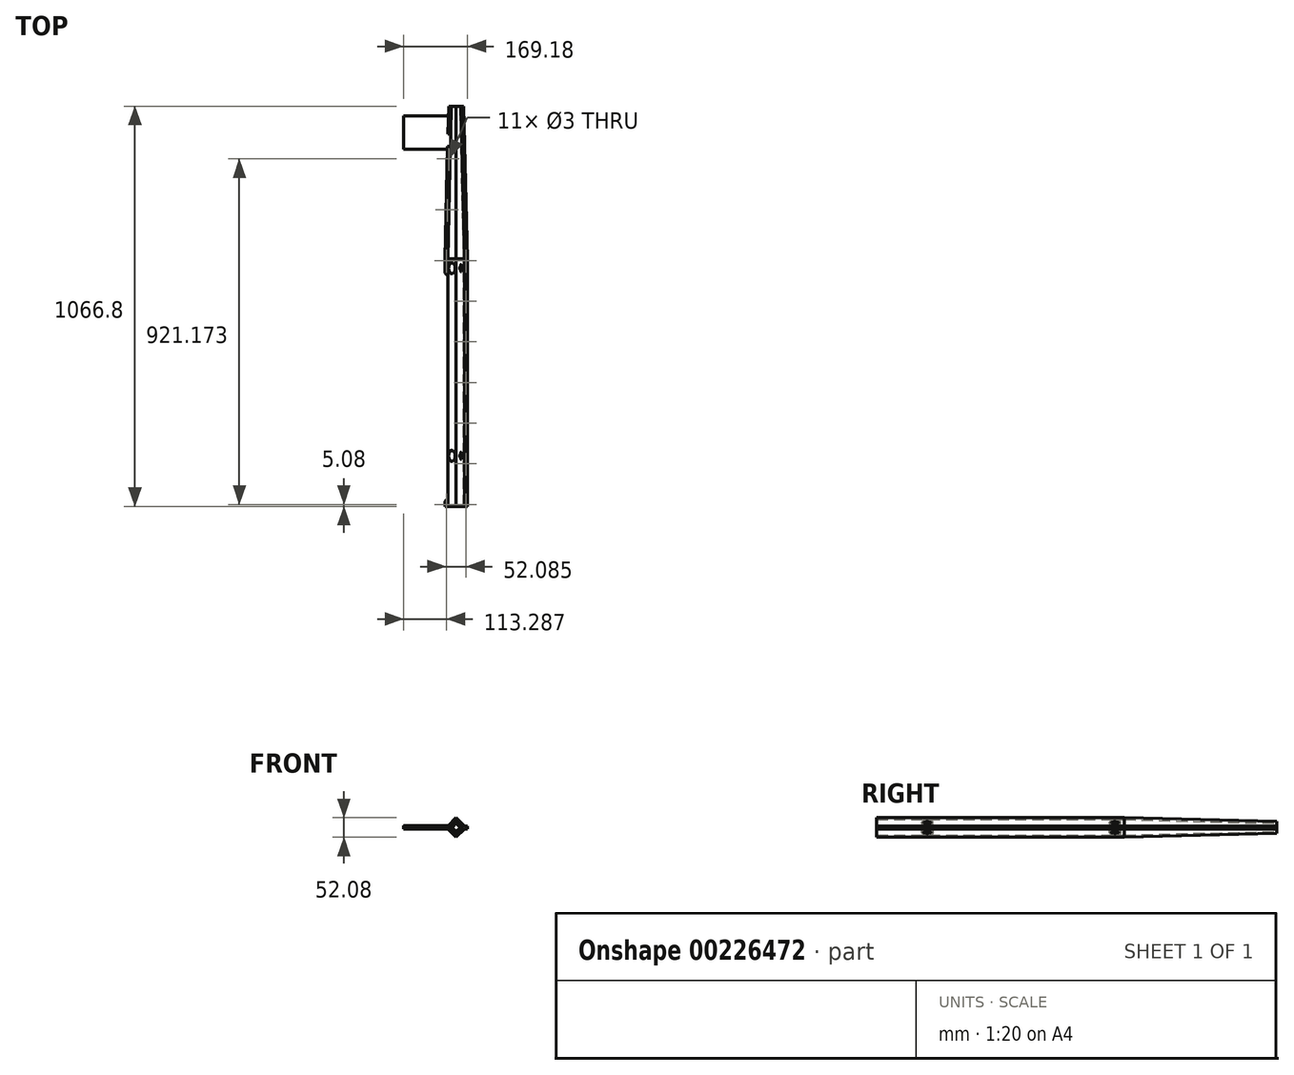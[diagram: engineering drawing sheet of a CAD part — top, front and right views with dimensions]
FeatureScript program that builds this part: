
annotation { "Feature Type Name" : "Feature", "Feature Type Description" : "" }
export const myFeature = defineFeature(function(context is Context, id is Id, definition is map)
    precondition{}
    {
        {
            var Q0;
            Q0=qCreatedBy(makeId("Front.planeOp"),FACE);
            var sketch = newSketch(context, id + "F0", { "sketchPlane" : qUnion([Q0])});
            skLineSegment(sketch, "E0", {"start": v(0, 0) * mm, "end": v(0, -26.04) * mm, "construction": true});
            skLineSegment(sketch, "E1", {"start": v(0, -20.65) * mm, "end": v(-20.65, 0) * mm});
            skLineSegment(sketch, "E2", {"start": v(0, -26.04) * mm, "end": v(-22.23, -3.81) * mm});
            skLineSegment(sketch, "E3", {"start": v(-22.23, -3.8) * mm, "end": v(-29.85, -3.81) * mm});
            skLineSegment(sketch, "E4", {"start": v(-29.85, -3.81) * mm, "end": v(-29.85, 0) * mm});
            skLineSegment(sketch, "E5", {"start": v(-29.85, 0) * mm, "end": v(-20.65, 0) * mm});
            skLineSegment(sketch, "E6.MirrorCS", {"start": v(29.85, -3.8) * mm, "end": v(29.85, 0) * mm});
            skLineSegment(sketch, "E7.MirrorCS", {"start": v(29.85, 0) * mm, "end": v(20.65, 0) * mm});
            skLineSegment(sketch, "E8.MirrorCS", {"start": v(0, -20.65) * mm, "end": v(20.65, 0) * mm});
            skLineSegment(sketch, "E9.MirrorCS", {"start": v(22.23, -3.8) * mm, "end": v(29.85, -3.8) * mm});
            skLineSegment(sketch, "E10.MirrorCS", {"start": v(0, -26.04) * mm, "end": v(22.23, -3.8) * mm});
            skSolve(sketch);
        }
        {
            var Q0;
            Q0=makeQuery(id+"F0.imprint","IMPRINT",FACE,{"disambiguationData":[TD([[makeQuery(id+"F0.imprint","IMPRINT",EDGE,{"derivedFrom":sQuery(id+"F0.wireOp",EDGE,"E1")}),1.0]])]});
            extrude(context, id + "F1", {"entities" : qUnion([Q0]), "depth" : 660.4 * mm});
        }
        {
            var Q0;
            Q0=makeQuery(id+"F1.opExtrude","SWEPT_FACE",FACE,{"disambiguationData":[OSD([sQuery(id+"F0.wireOp",EDGE,"E2")])]});
            var sketch = newSketch(context, id + "F2", { "sketchPlane" : qUnion([Q0])});
            skCircle(sketch, "E11", {"center": v(525.78, -0.79) * mm, "radius": 14.5 * mm});
            skCircle(sketch, "E12", {"center": v(25.4, -0.79) * mm, "radius": 14.5 * mm});
            skPoint(sketch, "E13.0", {"position": v(660.4, -14.6) * mm});
            skLineSegment(sketch, "E14", {"start": v(660.4, -14.6) * mm, "end": v(660.4, 13.03) * mm, "construction": true});
            skLineSegment(sketch, "E15", {"start": v(660.4, -0.79) * mm, "end": v(-254, -0.79) * mm, "construction": true});
            skSolve(sketch);
        }
        {
            var Q0;
            Q0=makeQuery(id+"F2.imprint","IMPRINT",FACE,{"disambiguationData":[TD([[makeQuery(id+"F2.imprint","IMPRINT",EDGE,{"derivedFrom":sQuery(id+"F2.wireOp",EDGE,"E11")}),1.0]])]});
            var Q1;
            Q1=makeQuery(id+"F2.imprint","IMPRINT",FACE,{"disambiguationData":[TD([[makeQuery(id+"F2.imprint","IMPRINT",EDGE,{"derivedFrom":sQuery(id+"F2.wireOp",EDGE,"E12")}),1.0]])]});
            var Q2;
            Q2=makeQuery(id+"F1.opExtrude","SWEPT_FACE",FACE,{"disambiguationData":[OSD([sQuery(id+"F0.wireOp",EDGE,"E1")])]});
            extrude(context, id + "F3", {"entities" : qUnion([Q0, Q1]), "operationType" : NewBodyOperationType.REMOVE, "endBound" : BoundingType.UP_TO_SURFACE, "oppositeDirection" : true, "endBoundEntityFace" : qUnion([Q2]), "depth" : 25.4 * mm});
        }
        {
            var Q0;
            Q0=makeQuery(id+"F1.opExtrude","SWEPT_FACE",FACE,{"disambiguationData":[OSD([sQuery(id+"F0.wireOp",EDGE,"E10.MirrorCS")])]});
            var sketch = newSketch(context, id + "F4", { "sketchPlane" : qUnion([Q0])});
            skCircle(sketch, "E16", {"center": v(-25.4, 0) * mm, "radius": 8 * mm, "construction": true});
            skPoint(sketch, "E16.centerSnap0", {"position": v(0, -2.7) * mm});
            skCircle(sketch, "E17", {"center": v(-33.4, 0) * mm, "radius": 1.5 * mm});
            skCircle(sketch, "E18", {"center": v(-17.4, 0) * mm, "radius": 1.5 * mm});
            skLineSegment(sketch, "E19", {"start": v(-17.4, 0) * mm, "end": v(-33.4, 0) * mm, "construction": true});
            skCircle(sketch, "E20", {"center": v(-525.78, 0) * mm, "radius": 8 * mm, "construction": true});
            skCircle(sketch, "E21", {"center": v(-533.78, 0) * mm, "radius": 1.5 * mm});
            skCircle(sketch, "E22", {"center": v(-517.78, 0) * mm, "radius": 1.5 * mm});
            skLineSegment(sketch, "E23", {"start": v(-517.78, 0) * mm, "end": v(-533.78, 0) * mm, "construction": true});
            skPoint(sketch, "E24", {"position": v(-660.4, -2.7) * mm});
            skCircle(sketch, "E25", {"center": v(-525.78, 0) * mm, "radius": 4.5 * mm});
            skCircle(sketch, "E26", {"center": v(-25.4, 0) * mm, "radius": 4.5 * mm});
            skSolve(sketch);
        }
        {
            var Q0;
            Q0 = qSketchRegion(id + "F4", true);
            var Q1;
            Q1=makeQuery(id+"F1.opExtrude","SWEPT_FACE",FACE,{"disambiguationData":[OSD([sQuery(id+"F0.wireOp",EDGE,"E8.MirrorCS")])]});
            extrude(context, id + "F5", {"entities" : qUnion([Q0]), "operationType" : NewBodyOperationType.REMOVE, "endBound" : BoundingType.UP_TO_SURFACE, "oppositeDirection" : true, "endBoundEntityFace" : qUnion([Q1]), "depth" : 25.4 * mm});
        }
        {
            var Q0;
            Q0=makeQuery(id+"F1.opExtrude","CAP_FACE",FACE,{"disambiguationData":[OSD([sQuery(id+"F0.wireOp",EDGE,"E1"),sQuery(id+"F0.wireOp",EDGE,"E2"),sQuery(id+"F0.wireOp",EDGE,"E3"),sQuery(id+"F0.wireOp",EDGE,"E4"),sQuery(id+"F0.wireOp",EDGE,"E5"),sQuery(id+"F0.wireOp",EDGE,"E6.MirrorCS"),sQuery(id+"F0.wireOp",EDGE,"E7.MirrorCS"),sQuery(id+"F0.wireOp",EDGE,"E8.MirrorCS"),sQuery(id+"F0.wireOp",EDGE,"E9.MirrorCS"),sQuery(id+"F0.wireOp",EDGE,"E10.MirrorCS")])],"isStart":true});
            cPlane(context, id + "F6", {"entities" : qUnion([Q0]), "cplaneType" : CPlaneType.OFFSET, "offset" : 406.4 * mm, "width" : 152.4 * mm, "height" : 152.4 * mm});
        }
        {
            var Q0;
            Q0=qCreatedBy(id+"F6.planeOp",FACE);
            var sketch = newSketch(context, id + "F7", { "sketchPlane" : qUnion([Q0])});
            skLineSegment(sketch, "E27.0.0", {"start": v(0, -26.04) * mm, "end": v(22.23, -3.81) * mm, "construction": true});
            skLineSegment(sketch, "E27.0.1", {"start": v(22.23, -3.8) * mm, "end": v(29.85, -3.81) * mm, "construction": true});
            skLineSegment(sketch, "E27.0.2", {"start": v(29.85, -3.81) * mm, "end": v(29.85, 0) * mm, "construction": true});
            skLineSegment(sketch, "E27.0.3", {"start": v(29.85, 0) * mm, "end": v(20.65, 0) * mm, "construction": true});
            skLineSegment(sketch, "E27.0.4", {"start": v(20.65, 0) * mm, "end": v(0, -20.65) * mm, "construction": true});
            skLineSegment(sketch, "E27.0.5", {"start": v(0, -20.65) * mm, "end": v(-20.65, 0) * mm, "construction": true});
            skLineSegment(sketch, "E27.0.6", {"start": v(-20.65, 0) * mm, "end": v(-29.85, 0) * mm, "construction": true});
            skLineSegment(sketch, "E27.0.7", {"start": v(-29.85, 0) * mm, "end": v(-29.85, -3.8) * mm, "construction": true});
            skLineSegment(sketch, "E27.0.8", {"start": v(-29.85, -3.8) * mm, "end": v(-22.23, -3.8) * mm, "construction": true});
            skLineSegment(sketch, "E27.0.9", {"start": v(-22.23, -3.8) * mm, "end": v(0, -26.04) * mm, "construction": true});
            skLineSegment(sketch, "E28", {"start": v(0, -26.04) * mm, "end": v(0, 0) * mm, "construction": true});
            skLineSegment(sketch, "E29", {"start": v(0, -16.16) * mm, "end": v(12.35, -3.8) * mm});
            skLineSegment(sketch, "E30", {"start": v(12.35, -3.81) * mm, "end": v(19.97, -3.81) * mm});
            skLineSegment(sketch, "E31", {"start": v(19.97, -3.8) * mm, "end": v(19.97, 0) * mm});
            skLineSegment(sketch, "E32", {"start": v(19.97, 0) * mm, "end": v(10.78, 0) * mm});
            skLineSegment(sketch, "E33", {"start": v(10.78, 0) * mm, "end": v(0, -10.78) * mm});
            skLineSegment(sketch, "E34", {"start": v(0, -10.78) * mm, "end": v(-10.78, 0) * mm});
            skLineSegment(sketch, "E35", {"start": v(-10.78, 0) * mm, "end": v(-19.97, 0) * mm});
            skLineSegment(sketch, "E36", {"start": v(-19.97, 0) * mm, "end": v(-19.97, -3.8) * mm});
            skLineSegment(sketch, "E37", {"start": v(-19.97, -3.81) * mm, "end": v(-12.35, -3.81) * mm});
            skLineSegment(sketch, "E38", {"start": v(-12.35, -3.8) * mm, "end": v(0, -16.16) * mm});
            skSolve(sketch);
        }
        {
            var Q1;
            Q1=makeQuery(id+"F1.opExtrude","CAP_FACE",FACE,{"disambiguationData":[OSD([sQuery(id+"F0.wireOp",EDGE,"E1"),sQuery(id+"F0.wireOp",EDGE,"E2"),sQuery(id+"F0.wireOp",EDGE,"E3"),sQuery(id+"F0.wireOp",EDGE,"E4"),sQuery(id+"F0.wireOp",EDGE,"E5"),sQuery(id+"F0.wireOp",EDGE,"E6.MirrorCS"),sQuery(id+"F0.wireOp",EDGE,"E7.MirrorCS"),sQuery(id+"F0.wireOp",EDGE,"E8.MirrorCS"),sQuery(id+"F0.wireOp",EDGE,"E9.MirrorCS"),sQuery(id+"F0.wireOp",EDGE,"E10.MirrorCS")])],"isStart":true});
            var Q2;
            Q2=makeQuery(id+"F7.imprint","IMPRINT",FACE,{"disambiguationData":[TD([[makeQuery(id+"F7.imprint","IMPRINT",EDGE,{"derivedFrom":sQuery(id+"F7.wireOp",EDGE,"E29")}),1.0]])]});
            loft(context, id + "F8", {"operationType" : NewBodyOperationType.ADD, "sheetProfilesArray" : [{ "sheetProfileEntities" : qUnion([Q1]) }, { "sheetProfileEntities" : qUnion([Q2]) }]});
        }
        {
            var Q0;
            Q0=makeQuery(id+"F1.opExtrude","SWEPT_BODY",BODY,{"disambiguationData":[OSD([sQuery(id+"F0.wireOp",EDGE,"E1"),sQuery(id+"F0.wireOp",EDGE,"E2"),sQuery(id+"F0.wireOp",EDGE,"E3"),sQuery(id+"F0.wireOp",EDGE,"E4"),sQuery(id+"F0.wireOp",EDGE,"E5"),sQuery(id+"F0.wireOp",EDGE,"E6.MirrorCS"),sQuery(id+"F0.wireOp",EDGE,"E7.MirrorCS"),sQuery(id+"F0.wireOp",EDGE,"E8.MirrorCS"),sQuery(id+"F0.wireOp",EDGE,"E9.MirrorCS"),sQuery(id+"F0.wireOp",EDGE,"E10.MirrorCS")])]});
            var Q1;
            Q1=qCreatedBy(makeId("Top.planeOp"),FACE);
            mirror(context, id + "F9", {"entities" : qUnion([Q0]), "mirrorPlane" : qUnion([Q1])});
        }
        {
            var Q0;
            Q0=makeQuery(id+"F1.opExtrude","SWEPT_FACE",FACE,{"disambiguationData":[OSD([sQuery(id+"F0.wireOp",EDGE,"E3")])]});
            var sketch = newSketch(context, id + "F10", { "sketchPlane" : qUnion([Q0])});
            skCircle(sketch, "E39.cCircle", {"center": v(-26.04, 5.08) * mm, "radius": 3 * mm, "construction": true});
            skPoint(sketch, "E39.cCircle.centerSnap0", {"position": v(-26.04, 0) * mm});
            skLineSegment(sketch, "E39.0", {"start": v(-23.04, 3.35) * mm, "end": v(-26.04, 1.62) * mm});
            skLineSegment(sketch, "E39.1", {"start": v(-26.04, 1.62) * mm, "end": v(-29.04, 3.35) * mm});
            skLineSegment(sketch, "E39.2", {"start": v(-29.04, 3.35) * mm, "end": v(-29.04, 6.81) * mm});
            skLineSegment(sketch, "E39.3", {"start": v(-29.04, 6.81) * mm, "end": v(-26.04, 8.54) * mm});
            skLineSegment(sketch, "E39.4", {"start": v(-26.04, 8.54) * mm, "end": v(-23.04, 6.81) * mm});
            skLineSegment(sketch, "E39.5", {"start": v(-23.04, 6.81) * mm, "end": v(-23.04, 3.35) * mm});
            skPoint(sketch, "E39.0.midPoint", {"position": v(-24.54, 2.48) * mm});
            skCircle(sketch, "E40.cCircle", {"center": v(26.04, 655.32) * mm, "radius": 3 * mm, "construction": true});
            skLineSegment(sketch, "E40.0", {"start": v(29.04, 653.59) * mm, "end": v(26.04, 651.86) * mm});
            skLineSegment(sketch, "E40.1", {"start": v(26.04, 651.86) * mm, "end": v(23.04, 653.59) * mm});
            skLineSegment(sketch, "E40.2", {"start": v(23.04, 653.59) * mm, "end": v(23.04, 657.05) * mm});
            skLineSegment(sketch, "E40.3", {"start": v(23.04, 657.05) * mm, "end": v(26.04, 658.78) * mm});
            skLineSegment(sketch, "E40.4", {"start": v(26.04, 658.78) * mm, "end": v(29.04, 657.05) * mm});
            skLineSegment(sketch, "E40.5", {"start": v(29.04, 657.05) * mm, "end": v(29.04, 653.59) * mm});
            skCircle(sketch, "E41.cCircle", {"center": v(-26.04, 655.32) * mm, "radius": 3 * mm, "construction": true});
            skLineSegment(sketch, "E41.0", {"start": v(-23.04, 653.59) * mm, "end": v(-26.04, 651.86) * mm});
            skLineSegment(sketch, "E41.1", {"start": v(-26.04, 651.86) * mm, "end": v(-29.04, 653.59) * mm});
            skLineSegment(sketch, "E41.2", {"start": v(-29.04, 653.59) * mm, "end": v(-29.04, 657.05) * mm});
            skLineSegment(sketch, "E41.3", {"start": v(-29.04, 657.05) * mm, "end": v(-26.04, 658.78) * mm});
            skLineSegment(sketch, "E41.4", {"start": v(-26.04, 658.78) * mm, "end": v(-23.04, 657.05) * mm});
            skLineSegment(sketch, "E41.5", {"start": v(-23.04, 657.05) * mm, "end": v(-23.04, 653.59) * mm});
            skCircle(sketch, "E42", {"center": v(-26.04, 5.08) * mm, "radius": 1.5 * mm});
            skCircle(sketch, "E43", {"center": v(26.04, 655.32) * mm, "radius": 1.5 * mm});
            skCircle(sketch, "E44", {"center": v(-26.04, 655.32) * mm, "radius": 1.5 * mm});
            skLineSegment(sketch, "E45.1.0.0", {"start": v(23.04, 548.68) * mm, "end": v(26.04, 550.41) * mm});
            skCircle(sketch, "E45.1.0.1", {"center": v(26.04, 546.95) * mm, "radius": 1.5 * mm});
            skLineSegment(sketch, "E45.1.0.2", {"start": v(26.04, 543.48) * mm, "end": v(23.04, 545.21) * mm});
            skLineSegment(sketch, "E45.1.0.3", {"start": v(26.04, 550.41) * mm, "end": v(29.04, 548.68) * mm});
            skLineSegment(sketch, "E45.1.0.4", {"start": v(29.04, 548.68) * mm, "end": v(29.04, 545.21) * mm});
            skCircle(sketch, "E45.1.0.5", {"center": v(26.04, 546.95) * mm, "radius": 3 * mm, "construction": true});
            skLineSegment(sketch, "E45.1.0.6", {"start": v(29.04, 545.21) * mm, "end": v(26.04, 543.48) * mm});
            skLineSegment(sketch, "E45.1.0.7", {"start": v(23.04, 545.21) * mm, "end": v(23.04, 548.68) * mm});
            skLineSegment(sketch, "E45.2.0.0", {"start": v(23.04, 440.3) * mm, "end": v(26.04, 442.04) * mm});
            skCircle(sketch, "E45.2.0.1", {"center": v(26.04, 438.57) * mm, "radius": 1.5 * mm});
            skLineSegment(sketch, "E45.2.0.2", {"start": v(26.04, 435.1) * mm, "end": v(23.04, 436.84) * mm});
            skLineSegment(sketch, "E45.2.0.3", {"start": v(26.04, 442.04) * mm, "end": v(29.04, 440.3) * mm});
            skLineSegment(sketch, "E45.2.0.4", {"start": v(29.04, 440.3) * mm, "end": v(29.04, 436.84) * mm});
            skCircle(sketch, "E45.2.0.5", {"center": v(26.04, 438.57) * mm, "radius": 3 * mm, "construction": true});
            skLineSegment(sketch, "E45.2.0.6", {"start": v(29.04, 436.84) * mm, "end": v(26.04, 435.1) * mm});
            skLineSegment(sketch, "E45.2.0.7", {"start": v(23.04, 436.84) * mm, "end": v(23.04, 440.3) * mm});
            skLineSegment(sketch, "E45.3.0.0", {"start": v(23.04, 331.93) * mm, "end": v(26.04, 333.66) * mm});
            skCircle(sketch, "E45.3.0.1", {"center": v(26.04, 330.2) * mm, "radius": 1.5 * mm});
            skLineSegment(sketch, "E45.3.0.2", {"start": v(26.04, 326.74) * mm, "end": v(23.04, 328.47) * mm});
            skLineSegment(sketch, "E45.3.0.3", {"start": v(26.04, 333.66) * mm, "end": v(29.04, 331.93) * mm});
            skLineSegment(sketch, "E45.3.0.4", {"start": v(29.04, 331.93) * mm, "end": v(29.04, 328.47) * mm});
            skCircle(sketch, "E45.3.0.5", {"center": v(26.04, 330.2) * mm, "radius": 3 * mm, "construction": true});
            skLineSegment(sketch, "E45.3.0.6", {"start": v(29.04, 328.47) * mm, "end": v(26.04, 326.74) * mm});
            skLineSegment(sketch, "E45.3.0.7", {"start": v(23.04, 328.47) * mm, "end": v(23.04, 331.93) * mm});
            skLineSegment(sketch, "E45.4.0.0", {"start": v(23.04, 223.56) * mm, "end": v(26.04, 225.3) * mm});
            skCircle(sketch, "E45.4.0.1", {"center": v(26.04, 221.83) * mm, "radius": 1.5 * mm});
            skLineSegment(sketch, "E45.4.0.2", {"start": v(26.04, 218.36) * mm, "end": v(23.04, 220.1) * mm});
            skLineSegment(sketch, "E45.4.0.3", {"start": v(26.04, 225.3) * mm, "end": v(29.04, 223.56) * mm});
            skLineSegment(sketch, "E45.4.0.4", {"start": v(29.04, 223.56) * mm, "end": v(29.04, 220.1) * mm});
            skCircle(sketch, "E45.4.0.5", {"center": v(26.04, 221.83) * mm, "radius": 3 * mm, "construction": true});
            skLineSegment(sketch, "E45.4.0.6", {"start": v(29.04, 220.1) * mm, "end": v(26.04, 218.36) * mm});
            skLineSegment(sketch, "E45.4.0.7", {"start": v(23.04, 220.1) * mm, "end": v(23.04, 223.56) * mm});
            skLineSegment(sketch, "E45.5.0.0", {"start": v(23.04, 115.19) * mm, "end": v(26.04, 116.92) * mm});
            skCircle(sketch, "E45.5.0.1", {"center": v(26.04, 113.45) * mm, "radius": 1.5 * mm});
            skLineSegment(sketch, "E45.5.0.2", {"start": v(26.04, 109.99) * mm, "end": v(23.04, 111.72) * mm});
            skLineSegment(sketch, "E45.5.0.3", {"start": v(26.04, 116.92) * mm, "end": v(29.04, 115.19) * mm});
            skLineSegment(sketch, "E45.5.0.4", {"start": v(29.04, 115.19) * mm, "end": v(29.04, 111.72) * mm});
            skCircle(sketch, "E45.5.0.5", {"center": v(26.04, 113.45) * mm, "radius": 3 * mm, "construction": true});
            skLineSegment(sketch, "E45.5.0.6", {"start": v(29.04, 111.72) * mm, "end": v(26.04, 109.99) * mm});
            skLineSegment(sketch, "E45.5.0.7", {"start": v(23.04, 111.72) * mm, "end": v(23.04, 115.19) * mm});
            skLineSegment(sketch, "E45.6.0.0", {"start": v(23.04, 6.81) * mm, "end": v(26.04, 8.54) * mm});
            skCircle(sketch, "E45.6.0.1", {"center": v(26.04, 5.08) * mm, "radius": 1.5 * mm});
            skLineSegment(sketch, "E45.6.0.2", {"start": v(26.04, 1.62) * mm, "end": v(23.04, 3.35) * mm});
            skLineSegment(sketch, "E45.6.0.3", {"start": v(26.04, 8.54) * mm, "end": v(29.04, 6.81) * mm});
            skLineSegment(sketch, "E45.6.0.4", {"start": v(29.04, 6.81) * mm, "end": v(29.04, 3.35) * mm});
            skCircle(sketch, "E45.6.0.5", {"center": v(26.04, 5.08) * mm, "radius": 3 * mm, "construction": true});
            skLineSegment(sketch, "E45.6.0.6", {"start": v(29.04, 3.35) * mm, "end": v(26.04, 1.62) * mm});
            skLineSegment(sketch, "E45.6.0.7", {"start": v(23.04, 3.35) * mm, "end": v(23.04, 6.81) * mm});
            skLineSegment(sketch, "E45.direction1", {"start": v(23.04, 653.59) * mm, "end": v(23.04, 545.21) * mm, "construction": true});
            skLineSegment(sketch, "E46", {"start": v(-22.23, 0) * mm, "end": v(-29.85, 0) * mm, "construction": true});
            skPoint(sketch, "E47.0", {"position": v(22.23, 0) * mm});
            skPoint(sketch, "E48.0", {"position": v(29.85, 0) * mm});
            skLineSegment(sketch, "E49", {"start": v(22.23, 0) * mm, "end": v(29.85, 0) * mm, "construction": true});
            skSolve(sketch);
        }
        {
            var Q0;
            Q0 = qSketchRegion(id + "F10", true);
            extrude(context, id + "F11", {"entities" : qUnion([Q0]), "operationType" : NewBodyOperationType.REMOVE, "oppositeDirection" : true, "depth" : 2.5 * mm});
        }
        {
            var Q0;
            Q0=makeQuery(id+"F11.boolean.opBoolean","SPLIT",FACE,{"disambiguationData":[TD([makeQuery(id+"F11.opExtrude","SWEPT_FACE",FACE,{"disambiguationData":[OSD([sQuery(id+"F10.wireOp",EDGE,"E43")])]})])],"derivedFrom":makeQuery(id+"F1.opExtrude","SWEPT_FACE",FACE,{"disambiguationData":[OSD([sQuery(id+"F0.wireOp",EDGE,"E9.MirrorCS")])]})});
            var Q1;
            Q1=makeQuery(id+"F11.boolean.opBoolean","SPLIT",FACE,{"disambiguationData":[TD([makeQuery(id+"F11.opExtrude","SWEPT_FACE",FACE,{"disambiguationData":[OSD([sQuery(id+"F10.wireOp",EDGE,"E45.1.0.1")])]})])],"derivedFrom":makeQuery(id+"F1.opExtrude","SWEPT_FACE",FACE,{"disambiguationData":[OSD([sQuery(id+"F0.wireOp",EDGE,"E9.MirrorCS")])]})});
            var Q2;
            Q2=makeQuery(id+"F11.boolean.opBoolean","SPLIT",FACE,{"disambiguationData":[TD([makeQuery(id+"F11.opExtrude","SWEPT_FACE",FACE,{"disambiguationData":[OSD([sQuery(id+"F10.wireOp",EDGE,"E44")])]})])],"derivedFrom":makeQuery(id+"F1.opExtrude","SWEPT_FACE",FACE,{"disambiguationData":[OSD([sQuery(id+"F0.wireOp",EDGE,"E3")])]})});
            var Q3;
            Q3=makeQuery(id+"F11.boolean.opBoolean","SPLIT",FACE,{"disambiguationData":[TD([makeQuery(id+"F11.opExtrude","SWEPT_FACE",FACE,{"disambiguationData":[OSD([sQuery(id+"F10.wireOp",EDGE,"E45.2.0.1")])]})])],"derivedFrom":makeQuery(id+"F1.opExtrude","SWEPT_FACE",FACE,{"disambiguationData":[OSD([sQuery(id+"F0.wireOp",EDGE,"E9.MirrorCS")])]})});
            var Q4;
            Q4=makeQuery(id+"F11.boolean.opBoolean","SPLIT",FACE,{"disambiguationData":[TD([makeQuery(id+"F11.opExtrude","SWEPT_FACE",FACE,{"disambiguationData":[OSD([sQuery(id+"F10.wireOp",EDGE,"E45.3.0.1")])]})])],"derivedFrom":makeQuery(id+"F1.opExtrude","SWEPT_FACE",FACE,{"disambiguationData":[OSD([sQuery(id+"F0.wireOp",EDGE,"E9.MirrorCS")])]})});
            var Q5;
            Q5=makeQuery(id+"F11.boolean.opBoolean","SPLIT",FACE,{"disambiguationData":[TD([makeQuery(id+"F11.opExtrude","SWEPT_FACE",FACE,{"disambiguationData":[OSD([sQuery(id+"F10.wireOp",EDGE,"E45.4.0.1")])]})])],"derivedFrom":makeQuery(id+"F1.opExtrude","SWEPT_FACE",FACE,{"disambiguationData":[OSD([sQuery(id+"F0.wireOp",EDGE,"E9.MirrorCS")])]})});
            var Q6;
            Q6=makeQuery(id+"F11.boolean.opBoolean","SPLIT",FACE,{"disambiguationData":[TD([makeQuery(id+"F11.opExtrude","SWEPT_FACE",FACE,{"disambiguationData":[OSD([sQuery(id+"F10.wireOp",EDGE,"E45.5.0.1")])]})])],"derivedFrom":makeQuery(id+"F1.opExtrude","SWEPT_FACE",FACE,{"disambiguationData":[OSD([sQuery(id+"F0.wireOp",EDGE,"E9.MirrorCS")])]})});
            var Q7;
            Q7=makeQuery(id+"F11.boolean.opBoolean","SPLIT",FACE,{"disambiguationData":[TD([makeQuery(id+"F11.opExtrude","SWEPT_FACE",FACE,{"disambiguationData":[OSD([sQuery(id+"F10.wireOp",EDGE,"E45.6.0.1")])]})])],"derivedFrom":makeQuery(id+"F1.opExtrude","SWEPT_FACE",FACE,{"disambiguationData":[OSD([sQuery(id+"F0.wireOp",EDGE,"E9.MirrorCS")])]})});
            var Q8;
            Q8=makeQuery(id+"F11.boolean.opBoolean","SPLIT",FACE,{"disambiguationData":[TD([makeQuery(id+"F11.opExtrude","SWEPT_FACE",FACE,{"disambiguationData":[OSD([sQuery(id+"F10.wireOp",EDGE,"E45.7.0.1")])]})])],"derivedFrom":makeQuery(id+"F1.opExtrude","SWEPT_FACE",FACE,{"disambiguationData":[OSD([sQuery(id+"F0.wireOp",EDGE,"E9.MirrorCS")])]})});
            var Q9;
            Q9=makeQuery(id+"F11.boolean.opBoolean","SPLIT",FACE,{"disambiguationData":[TD([makeQuery(id+"F11.opExtrude","SWEPT_FACE",FACE,{"disambiguationData":[OSD([sQuery(id+"F10.wireOp",EDGE,"E45.8.0.1")])]})])],"derivedFrom":makeQuery(id+"F1.opExtrude","SWEPT_FACE",FACE,{"disambiguationData":[OSD([sQuery(id+"F0.wireOp",EDGE,"E9.MirrorCS")])]})});
            var Q10;
            Q10=makeQuery(id+"F11.boolean.opBoolean","SPLIT",FACE,{"disambiguationData":[TD([makeQuery(id+"F11.opExtrude","SWEPT_FACE",FACE,{"disambiguationData":[OSD([sQuery(id+"F10.wireOp",EDGE,"E45.9.0.1")])]})])],"derivedFrom":makeQuery(id+"F1.opExtrude","SWEPT_FACE",FACE,{"disambiguationData":[OSD([sQuery(id+"F0.wireOp",EDGE,"E9.MirrorCS")])]})});
            var Q11;
            Q11=makeQuery(id+"F11.boolean.opBoolean","SPLIT",FACE,{"disambiguationData":[TD([makeQuery(id+"F11.opExtrude","SWEPT_FACE",FACE,{"disambiguationData":[OSD([sQuery(id+"F10.wireOp",EDGE,"E45.10.0.1")])]})])],"derivedFrom":makeQuery(id+"F1.opExtrude","SWEPT_FACE",FACE,{"disambiguationData":[OSD([sQuery(id+"F0.wireOp",EDGE,"E9.MirrorCS")])]})});
            var Q12;
            Q12=makeQuery(id+"F11.boolean.opBoolean","SPLIT",FACE,{"disambiguationData":[TD([makeQuery(id+"F11.opExtrude","SWEPT_FACE",FACE,{"disambiguationData":[OSD([sQuery(id+"F10.wireOp",EDGE,"E42")])]})])],"derivedFrom":makeQuery(id+"F1.opExtrude","SWEPT_FACE",FACE,{"disambiguationData":[OSD([sQuery(id+"F0.wireOp",EDGE,"E3")])]})});
            extrude(context, id + "F12", {"entities" : qUnion([Q0, Q1, Q2, Q3, Q4, Q5, Q6, Q7, Q8, Q9, Q10, Q11, Q12]), "operationType" : NewBodyOperationType.REMOVE, "endBound" : BoundingType.THROUGH_ALL, "oppositeDirection" : true, "depth" : 25.4 * mm});
        }
        {
            var Q0;
            Q0=makeQuery(id+"F1.opExtrude","SWEPT_FACE",FACE,{"disambiguationData":[OSD([sQuery(id+"F0.wireOp",EDGE,"E4")])]});
            var sketch = newSketch(context, id + "F13", { "sketchPlane" : qUnion([Q0])});
            skFitSpline(sketch, "E50", {"points": [v(-381, 0) * mm, v(-292.1, 0) * mm], "startDerivative": vector(96.86, 5.77) * mm, "endDerivative": vector(12.2, -28.1) * mm});
            skLineSegment(sketch, "E51", {"start": v(-381, 0) * mm, "end": v(-292.1, 0) * mm});
            skFitSpline(sketch, "E52.MirrorCS", {"points": [v(-381, 0) * mm, v(-292.1, 0) * mm], "startDerivative": vector(96.86, -5.77) * mm, "endDerivative": vector(12.2, 28.1) * mm});
            skLineSegment(sketch, "E53.MirrorCS", {"start": v(-381, 0) * mm, "end": v(-292.1, 0) * mm, "construction": true});
            skSolve(sketch);
        }
        {
            var Q0;
            Q0=makeQuery(id+"F13.imprint","IMPRINT",FACE,{"disambiguationData":[TD([[makeQuery(id+"F13.imprint","IMPRINT",EDGE,{"derivedFrom":sQuery(id+"F13.wireOp",EDGE,"E50")}),-1.0]])]});
            extrude(context, id + "F14", {"entities" : qUnion([Q0]), "operationType" : NewBodyOperationType.ADD, "depth" : 35.05 * mm, "symmetric" : true});
        }
        {
            var Q0;
            Q0=makeQuery(id+"F13.imprint","IMPRINT",FACE,{"disambiguationData":[TD([[makeQuery(id+"F13.imprint","IMPRINT",EDGE,{"derivedFrom":sQuery(id+"F13.wireOp",EDGE,"E51")}),-1.0]])]});
            extrude(context, id + "F15", {"entities" : qUnion([Q0]), "operationType" : NewBodyOperationType.ADD, "depth" : 35.05 * mm, "symmetric" : true});
        }
        {
            var Q0;
            Q0=makeQuery(id+"F15.opExtrude","CAP_FACE",FACE,{"disambiguationData":[OSD([sQuery(id+"F13.wireOp",EDGE,"E51"),sQuery(id+"F13.wireOp",EDGE,"E52.MirrorCS")])],"isStart":false});
            var Q1;
            Q1=makeQuery(id+"F14.opExtrude","CAP_FACE",FACE,{"disambiguationData":[OSD([sQuery(id+"F13.wireOp",EDGE,"E50"),sQuery(id+"F13.wireOp",EDGE,"E51")])],"isStart":false});
            extrude(context, id + "F16", {"entities" : qUnion([Q0, Q1]), "operationType" : NewBodyOperationType.ADD, "depth" : 91.95 * mm});
        }
        {
            var Q0;
            {var subQ1=sQuery(id+"F0.wireOp",EDGE,"E4");var subQ6=sQuery(id+"F7.wireOp",EDGE,"E31");var subQ7=sQuery(id+"F7.wireOp",EDGE,"E30");var subQ9=sQuery(id+"F0.wireOp",EDGE,"E3");var subQ17=sQuery(id+"F0.wireOp",EDGE,"E2");var subQ22=makeQuery(id+"F1.opExtrude","SWEPT_FACE",FACE,{"disambiguationData":[OSD([subQ17])]});var subQ27=sQuery(id+"F7.wireOp",EDGE,"E29");Q0=makeQuery(id+"F15.boolean.opBoolean","SPLIT",FACE,{"disambiguationData":[TD([subQ22])],"derivedFrom":makeQuery(id+"F8.boolean.opBoolean","MERGE",FACE,{"derivedFrom":[makeQuery(id+"F11.boolean.opBoolean","SPLIT",FACE,{"disambiguationData":[TD([subQ22])],"derivedFrom":makeQuery(id+"F1.opExtrude","SWEPT_FACE",FACE,{"disambiguationData":[OSD([subQ9])]})}),makeQuery(id+"F8.opLoft","SWEPT_FACE",FACE,{"disambiguationData":[OSD([subQ17,subQ9,subQ1,subQ27,subQ7,subQ6])]})]})});}
            var sketch = newSketch(context, id + "F17", { "sketchPlane" : qUnion([Q0])});
            skLineSegment(sketch, "E54.bottom", {"start": v(-29.85, 38.1) * mm, "end": v(-22.23, 38.1) * mm});
            skLineSegment(sketch, "E54.top", {"start": v(-29.85, 647.7) * mm, "end": v(-22.23, 647.7) * mm});
            skLineSegment(sketch, "E54.left", {"start": v(-29.85, 38.1) * mm, "end": v(-29.85, 647.7) * mm});
            skPoint(sketch, "E55.0", {"position": v(-12.46, 525.78) * mm});
            skPoint(sketch, "E56.0", {"position": v(-12.46, 25.4) * mm});
            skLineSegment(sketch, "E57", {"start": v(-12.46, 25.4) * mm, "end": v(-29.85, 25.4) * mm, "construction": true});
            skLineSegment(sketch, "E58", {"start": v(-26.04, 38.1) * mm, "end": v(-26.04, 25.4) * mm, "construction": true});
            skLineSegment(sketch, "E59", {"start": v(-26.04, 647.7) * mm, "end": v(-26.04, 660.4) * mm, "construction": true});
            skLineSegment(sketch, "E60.0", {"start": v(-29.85, 660.4) * mm, "end": v(-29.85, 648.75) * mm});
            skLineSegment(sketch, "E61.trimOffspring", {"start": v(-29.85, 37.05) * mm, "end": v(-29.85, 0) * mm});
            skLineSegment(sketch, "E62", {"start": v(-22.23, 639.03) * mm, "end": v(-22.23, 46.77) * mm});
            skLineSegment(sketch, "E63", {"start": v(-29.1, 38.84) * mm, "end": v(-22.98, 44.98) * mm});
            skPoint(sketch, "E64.visualSharp", {"position": v(-22.23, 45.72) * mm});
            skArc(sketch, "E64.filletArc", {"start": v(-22.98, 44.98) * mm, "mid": v(-22.43, 45.8) * mm, "end": v(-22.23, 46.77) * mm});
            skPoint(sketch, "E65.visualSharp", {"position": v(-29.85, 647.7) * mm});
            skArc(sketch, "E65.filletArc", {"start": v(-29.85, 647.7) * mm, "mid": v(-34.93, 647.62) * mm, "end": v(-29.85, 647.55) * mm});
            skLineSegment(sketch, "E66", {"start": v(-22.98, 640.82) * mm, "end": v(-29.1, 646.96) * mm});
            skPoint(sketch, "E67.visualSharp", {"position": v(-22.23, 640.08) * mm});
            skArc(sketch, "E67.filletArc", {"start": v(-22.23, 639.03) * mm, "mid": v(-22.43, 640) * mm, "end": v(-22.98, 640.82) * mm});
            skArc(sketch, "E68.filletArc", {"start": v(-29.85, 648.75) * mm, "mid": v(-29.66, 647.78) * mm, "end": v(-29.1, 646.96) * mm});
            skPoint(sketch, "E69.visualSharp", {"position": v(-29.85, 38.1) * mm});
            skArc(sketch, "E69.filletArc", {"start": v(-29.1, 38.84) * mm, "mid": v(-29.66, 38.02) * mm, "end": v(-29.85, 37.05) * mm});
            skSolve(sketch);
        }
        {
            var Q0;
            Q0=makeQuery(id+"F17.imprint","IMPRINT",FACE,{"disambiguationData":[TD([[makeQuery(id+"F17.imprint","IMPRINT",EDGE,{"derivedFrom":sQuery(id+"F17.wireOp",EDGE,"E54.left")}),1.0]])]});
            var Q1;
            {var subQ0=sQuery(id+"F17.wireOp",EDGE,"E54.bottom");var subQ3=sQuery(id+"F17.wireOp",EDGE,"E69.filletArc");var subQ4=makeQuery(id+"F17.imprint","INTERSECT",VERTEX,{"derivedFrom":[subQ0,subQ3]});Q1=makeQuery(id+"F17.imprint","IMPRINT",FACE,{"disambiguationData":[TD([[makeQuery(id+"F17.imprint","IMPRINT",EDGE,{"disambiguationData":[TD([[subQ4,1.0]])],"derivedFrom":subQ0}),-1.0]])]});}
            var Q2;
            {var subQ0=sQuery(id+"F17.wireOp",EDGE,"E54.top");var subQ3=sQuery(id+"F17.wireOp",EDGE,"E68.filletArc");var subQ4=makeQuery(id+"F17.imprint","INTERSECT",VERTEX,{"derivedFrom":[subQ0,subQ3]});Q2=makeQuery(id+"F17.imprint","IMPRINT",FACE,{"disambiguationData":[TD([[makeQuery(id+"F17.imprint","IMPRINT",EDGE,{"disambiguationData":[TD([[subQ4,1.0]])],"derivedFrom":subQ3}),-1.0]])]});}
            extrude(context, id + "F18", {"entities" : qUnion([Q0, Q1, Q2]), "operationType" : NewBodyOperationType.REMOVE, "endBound" : BoundingType.THROUGH_ALL, "oppositeDirection" : true, "depth" : 25.4 * mm});
        }
        {
            var Q0;
            {var subQ0=sQuery(id+"F0.wireOp",EDGE,"E10.MirrorCS");var subQ1=sQuery(id+"F0.wireOp",EDGE,"E9.MirrorCS");var subQ2=sQuery(id+"F0.wireOp",EDGE,"E6.MirrorCS");Q0=makeQuery(id+"F8.boolean.opBoolean","MERGE",FACE,{"derivedFrom":[makeQuery(id+"F11.boolean.opBoolean","SPLIT",FACE,{"disambiguationData":[TD([makeQuery(id+"F1.opExtrude","SWEPT_FACE",FACE,{"disambiguationData":[OSD([subQ2])]})])],"derivedFrom":makeQuery(id+"F1.opExtrude","SWEPT_FACE",FACE,{"disambiguationData":[OSD([subQ1])]})}),makeQuery(id+"F8.opLoft","SWEPT_FACE",FACE,{"disambiguationData":[OSD([subQ2,subQ1,subQ0,sQuery(id+"F7.wireOp",EDGE,"E36"),sQuery(id+"F7.wireOp",EDGE,"E37"),sQuery(id+"F7.wireOp",EDGE,"E38")])]})]});}
            var sketch = newSketch(context, id + "F19", { "sketchPlane" : qUnion([Q0])});
            skLineSegment(sketch, "E70.0", {"start": v(-23.04, 3.35) * mm, "end": v(-26.04, 1.62) * mm, "construction": true});
            skLineSegment(sketch, "E70.1", {"start": v(-23.04, 6.81) * mm, "end": v(-23.04, 3.35) * mm, "construction": true});
            skLineSegment(sketch, "E70.2", {"start": v(-26.04, 8.54) * mm, "end": v(-23.04, 6.81) * mm, "construction": true});
            skLineSegment(sketch, "E70.3", {"start": v(-29.04, 6.81) * mm, "end": v(-26.04, 8.54) * mm, "construction": true});
            skLineSegment(sketch, "E70.4", {"start": v(-29.04, 3.35) * mm, "end": v(-29.04, 6.81) * mm, "construction": true});
            skLineSegment(sketch, "E70.5", {"start": v(-26.04, 1.62) * mm, "end": v(-29.04, 3.35) * mm, "construction": true});
            skCircle(sketch, "E70.6", {"center": v(-26.04, 5.08) * mm, "radius": 1.5 * mm, "construction": true});
            skLineSegment(sketch, "E71.1.0.0", {"start": v(-25.75, -128.65) * mm, "end": v(-22.75, -126.92) * mm});
            skLineSegment(sketch, "E71.1.0.1", {"start": v(-19.75, -128.65) * mm, "end": v(-19.75, -132.12) * mm});
            skLineSegment(sketch, "E71.1.0.2", {"start": v(-22.75, -126.92) * mm, "end": v(-19.75, -128.65) * mm});
            skLineSegment(sketch, "E71.1.0.3", {"start": v(-19.75, -132.12) * mm, "end": v(-22.75, -133.85) * mm});
            skLineSegment(sketch, "E71.1.0.4", {"start": v(-25.75, -132.12) * mm, "end": v(-25.75, -128.65) * mm});
            skLineSegment(sketch, "E71.1.0.5", {"start": v(-22.75, -133.85) * mm, "end": v(-25.75, -132.12) * mm});
            skCircle(sketch, "E71.1.0.6", {"center": v(-22.75, -130.39) * mm, "radius": 1.5 * mm});
            skLineSegment(sketch, "E71.2.0.0", {"start": v(-22.46, -264.12) * mm, "end": v(-19.46, -262.39) * mm});
            skLineSegment(sketch, "E71.2.0.1", {"start": v(-16.46, -264.12) * mm, "end": v(-16.46, -267.59) * mm});
            skLineSegment(sketch, "E71.2.0.2", {"start": v(-19.46, -262.39) * mm, "end": v(-16.46, -264.12) * mm});
            skLineSegment(sketch, "E71.2.0.3", {"start": v(-16.46, -267.59) * mm, "end": v(-19.46, -269.32) * mm});
            skLineSegment(sketch, "E71.2.0.4", {"start": v(-22.46, -267.59) * mm, "end": v(-22.46, -264.12) * mm});
            skLineSegment(sketch, "E71.2.0.5", {"start": v(-19.46, -269.32) * mm, "end": v(-22.46, -267.59) * mm});
            skCircle(sketch, "E71.2.0.6", {"center": v(-19.46, -265.85) * mm, "radius": 1.5 * mm});
            skLineSegment(sketch, "E71.3.0.0", {"start": v(-19.16, -399.59) * mm, "end": v(-16.16, -397.86) * mm});
            skLineSegment(sketch, "E71.3.0.1", {"start": v(-13.16, -399.59) * mm, "end": v(-13.16, -403.05) * mm});
            skLineSegment(sketch, "E71.3.0.2", {"start": v(-16.16, -397.86) * mm, "end": v(-13.16, -399.59) * mm});
            skLineSegment(sketch, "E71.3.0.3", {"start": v(-13.16, -403.05) * mm, "end": v(-16.16, -404.78) * mm});
            skLineSegment(sketch, "E71.3.0.4", {"start": v(-19.16, -403.05) * mm, "end": v(-19.16, -399.59) * mm});
            skLineSegment(sketch, "E71.3.0.5", {"start": v(-16.16, -404.78) * mm, "end": v(-19.16, -403.05) * mm});
            skCircle(sketch, "E71.3.0.6", {"center": v(-16.16, -401.32) * mm, "radius": 1.5 * mm});
            skLineSegment(sketch, "E71.direction1", {"start": v(-29.04, 3.35) * mm, "end": v(-25.75, -132.12) * mm, "construction": true});
            skLineSegment(sketch, "E72.0", {"start": v(29.04, 3.35) * mm, "end": v(26.04, 1.62) * mm});
            skLineSegment(sketch, "E72.1", {"start": v(29.04, 6.81) * mm, "end": v(29.04, 3.35) * mm});
            skLineSegment(sketch, "E72.2", {"start": v(26.04, 8.54) * mm, "end": v(29.04, 6.81) * mm});
            skLineSegment(sketch, "E72.3", {"start": v(23.04, 6.81) * mm, "end": v(26.04, 8.54) * mm});
            skLineSegment(sketch, "E72.4", {"start": v(23.04, 3.35) * mm, "end": v(23.04, 6.81) * mm});
            skLineSegment(sketch, "E72.5", {"start": v(26.04, 1.62) * mm, "end": v(23.04, 3.35) * mm});
            skCircle(sketch, "E72.6", {"center": v(26.04, 5.08) * mm, "radius": 1.5 * mm});
            skCircle(sketch, "E73.1.0.0", {"center": v(22.75, -130.39) * mm, "radius": 1.5 * mm});
            skLineSegment(sketch, "E73.1.0.1", {"start": v(25.75, -132.12) * mm, "end": v(22.75, -133.85) * mm});
            skLineSegment(sketch, "E73.1.0.2", {"start": v(22.75, -126.92) * mm, "end": v(25.75, -128.65) * mm});
            skLineSegment(sketch, "E73.1.0.3", {"start": v(25.75, -128.65) * mm, "end": v(25.75, -132.12) * mm});
            skLineSegment(sketch, "E73.1.0.4", {"start": v(22.75, -133.85) * mm, "end": v(19.75, -132.12) * mm});
            skLineSegment(sketch, "E73.1.0.5", {"start": v(19.75, -132.12) * mm, "end": v(19.75, -128.65) * mm});
            skLineSegment(sketch, "E73.1.0.6", {"start": v(19.75, -128.65) * mm, "end": v(22.75, -126.92) * mm});
            skCircle(sketch, "E73.2.0.0", {"center": v(19.46, -265.85) * mm, "radius": 1.5 * mm});
            skLineSegment(sketch, "E73.2.0.1", {"start": v(22.46, -267.59) * mm, "end": v(19.46, -269.32) * mm});
            skLineSegment(sketch, "E73.2.0.2", {"start": v(19.46, -262.39) * mm, "end": v(22.46, -264.12) * mm});
            skLineSegment(sketch, "E73.2.0.3", {"start": v(22.46, -264.12) * mm, "end": v(22.46, -267.59) * mm});
            skLineSegment(sketch, "E73.2.0.4", {"start": v(19.46, -269.32) * mm, "end": v(16.46, -267.59) * mm});
            skLineSegment(sketch, "E73.2.0.5", {"start": v(16.46, -267.59) * mm, "end": v(16.46, -264.12) * mm});
            skLineSegment(sketch, "E73.2.0.6", {"start": v(16.46, -264.12) * mm, "end": v(19.46, -262.39) * mm});
            skCircle(sketch, "E73.3.0.0", {"center": v(16.16, -401.32) * mm, "radius": 1.5 * mm});
            skLineSegment(sketch, "E73.3.0.1", {"start": v(19.16, -403.05) * mm, "end": v(16.16, -404.78) * mm});
            skLineSegment(sketch, "E73.3.0.2", {"start": v(16.16, -397.86) * mm, "end": v(19.16, -399.59) * mm});
            skLineSegment(sketch, "E73.3.0.3", {"start": v(19.16, -399.59) * mm, "end": v(19.16, -403.05) * mm});
            skLineSegment(sketch, "E73.3.0.4", {"start": v(16.16, -404.78) * mm, "end": v(13.16, -403.05) * mm});
            skLineSegment(sketch, "E73.3.0.5", {"start": v(13.16, -403.05) * mm, "end": v(13.16, -399.59) * mm});
            skLineSegment(sketch, "E73.3.0.6", {"start": v(13.16, -399.59) * mm, "end": v(16.16, -397.86) * mm});
            skLineSegment(sketch, "E73.direction1", {"start": v(23.04, 3.35) * mm, "end": v(19.75, -132.12) * mm, "construction": true});
            skSolve(sketch);
        }
        {
            var Q0;
            Q0 = qSketchRegion(id + "F19", true);
            extrude(context, id + "F20", {"entities" : qUnion([Q0]), "operationType" : NewBodyOperationType.REMOVE, "oppositeDirection" : true, "depth" : 2.5 * mm});
        }
        {
            var Q0;
            {var subQ4=sQuery(id+"F0.wireOp",EDGE,"E2");var subQ5=makeQuery(id+"F1.opExtrude","SWEPT_FACE",FACE,{"disambiguationData":[OSD([subQ4])]});var subQ14=sQuery(id+"F0.wireOp",EDGE,"E4");var subQ18=sQuery(id+"F2.wireOp",EDGE,"E12");var subQ19=makeQuery(id+"F3.boolean.opBoolean","COPY",FACE,{"derivedFrom":makeQuery(id+"F3.opExtrude","SWEPT_FACE",FACE,{"disambiguationData":[OSD([subQ18])]})});var subQ21=sQuery(id+"F7.wireOp",EDGE,"E30");var subQ22=sQuery(id+"F7.wireOp",EDGE,"E29");var subQ24=sQuery(id+"F0.wireOp",EDGE,"E3");var subQ26=sQuery(id+"F7.wireOp",EDGE,"E31");Q0=makeQuery(id+"F20.boolean.opBoolean","SPLIT",FACE,{"disambiguationData":[TD([makeQuery(id+"F20.opExtrude","SWEPT_FACE",FACE,{"disambiguationData":[OSD([sQuery(id+"F19.wireOp",EDGE,"E71.1.0.6")])]})])],"derivedFrom":makeQuery(id+"F18.boolean.opBoolean","SPLIT",FACE,{"disambiguationData":[TD([subQ19])],"derivedFrom":makeQuery(id+"F15.boolean.opBoolean","SPLIT",FACE,{"disambiguationData":[TD([subQ5])],"derivedFrom":makeQuery(id+"F8.boolean.opBoolean","MERGE",FACE,{"derivedFrom":[makeQuery(id+"F11.boolean.opBoolean","SPLIT",FACE,{"disambiguationData":[TD([subQ5])],"derivedFrom":makeQuery(id+"F1.opExtrude","SWEPT_FACE",FACE,{"disambiguationData":[OSD([subQ24])]})}),makeQuery(id+"F8.opLoft","SWEPT_FACE",FACE,{"disambiguationData":[OSD([subQ4,subQ24,subQ14,subQ22,subQ21,subQ26])]})]})})})});}
            var Q1;
            {var subQ0=sQuery(id+"F0.wireOp",EDGE,"E10.MirrorCS");var subQ1=sQuery(id+"F0.wireOp",EDGE,"E9.MirrorCS");var subQ2=sQuery(id+"F0.wireOp",EDGE,"E6.MirrorCS");Q1=makeQuery(id+"F20.boolean.opBoolean","SPLIT",FACE,{"disambiguationData":[TD([makeQuery(id+"F20.opExtrude","SWEPT_FACE",FACE,{"disambiguationData":[OSD([sQuery(id+"F19.wireOp",EDGE,"e9320bb9-dfa5-404e-80d7-207bc9714f88.1.0.0")])]})])],"derivedFrom":makeQuery(id+"F8.boolean.opBoolean","MERGE",FACE,{"derivedFrom":[makeQuery(id+"F11.boolean.opBoolean","SPLIT",FACE,{"disambiguationData":[TD([makeQuery(id+"F1.opExtrude","SWEPT_FACE",FACE,{"disambiguationData":[OSD([subQ2])]})])],"derivedFrom":makeQuery(id+"F1.opExtrude","SWEPT_FACE",FACE,{"disambiguationData":[OSD([subQ1])]})}),makeQuery(id+"F8.opLoft","SWEPT_FACE",FACE,{"disambiguationData":[OSD([subQ2,subQ1,subQ0,sQuery(id+"F7.wireOp",EDGE,"E36"),sQuery(id+"F7.wireOp",EDGE,"E37"),sQuery(id+"F7.wireOp",EDGE,"E38")])]})]})});}
            var Q2;
            {var subQ0=sQuery(id+"F0.wireOp",EDGE,"E10.MirrorCS");var subQ1=sQuery(id+"F0.wireOp",EDGE,"E9.MirrorCS");var subQ2=sQuery(id+"F0.wireOp",EDGE,"E6.MirrorCS");Q2=makeQuery(id+"F20.boolean.opBoolean","SPLIT",FACE,{"disambiguationData":[TD([makeQuery(id+"F20.opExtrude","SWEPT_FACE",FACE,{"disambiguationData":[OSD([sQuery(id+"F19.wireOp",EDGE,"e9320bb9-dfa5-404e-80d7-207bc9714f88.2.0.0")])]})])],"derivedFrom":makeQuery(id+"F8.boolean.opBoolean","MERGE",FACE,{"derivedFrom":[makeQuery(id+"F11.boolean.opBoolean","SPLIT",FACE,{"disambiguationData":[TD([makeQuery(id+"F1.opExtrude","SWEPT_FACE",FACE,{"disambiguationData":[OSD([subQ2])]})])],"derivedFrom":makeQuery(id+"F1.opExtrude","SWEPT_FACE",FACE,{"disambiguationData":[OSD([subQ1])]})}),makeQuery(id+"F8.opLoft","SWEPT_FACE",FACE,{"disambiguationData":[OSD([subQ2,subQ1,subQ0,sQuery(id+"F7.wireOp",EDGE,"E36"),sQuery(id+"F7.wireOp",EDGE,"E37"),sQuery(id+"F7.wireOp",EDGE,"E38")])]})]})});}
            var Q3;
            {var subQ4=sQuery(id+"F0.wireOp",EDGE,"E2");var subQ5=makeQuery(id+"F1.opExtrude","SWEPT_FACE",FACE,{"disambiguationData":[OSD([subQ4])]});var subQ14=sQuery(id+"F0.wireOp",EDGE,"E4");var subQ18=sQuery(id+"F2.wireOp",EDGE,"E12");var subQ19=makeQuery(id+"F3.boolean.opBoolean","COPY",FACE,{"derivedFrom":makeQuery(id+"F3.opExtrude","SWEPT_FACE",FACE,{"disambiguationData":[OSD([subQ18])]})});var subQ21=sQuery(id+"F7.wireOp",EDGE,"E30");var subQ22=sQuery(id+"F7.wireOp",EDGE,"E29");var subQ24=sQuery(id+"F0.wireOp",EDGE,"E3");var subQ26=sQuery(id+"F7.wireOp",EDGE,"E31");Q3=makeQuery(id+"F20.boolean.opBoolean","SPLIT",FACE,{"disambiguationData":[TD([makeQuery(id+"F20.opExtrude","SWEPT_FACE",FACE,{"disambiguationData":[OSD([sQuery(id+"F19.wireOp",EDGE,"E71.2.0.6")])]})])],"derivedFrom":makeQuery(id+"F18.boolean.opBoolean","SPLIT",FACE,{"disambiguationData":[TD([subQ19])],"derivedFrom":makeQuery(id+"F15.boolean.opBoolean","SPLIT",FACE,{"disambiguationData":[TD([subQ5])],"derivedFrom":makeQuery(id+"F8.boolean.opBoolean","MERGE",FACE,{"derivedFrom":[makeQuery(id+"F11.boolean.opBoolean","SPLIT",FACE,{"disambiguationData":[TD([subQ5])],"derivedFrom":makeQuery(id+"F1.opExtrude","SWEPT_FACE",FACE,{"disambiguationData":[OSD([subQ24])]})}),makeQuery(id+"F8.opLoft","SWEPT_FACE",FACE,{"disambiguationData":[OSD([subQ4,subQ24,subQ14,subQ22,subQ21,subQ26])]})]})})})});}
            var Q4;
            {var subQ4=sQuery(id+"F0.wireOp",EDGE,"E2");var subQ5=makeQuery(id+"F1.opExtrude","SWEPT_FACE",FACE,{"disambiguationData":[OSD([subQ4])]});var subQ14=sQuery(id+"F0.wireOp",EDGE,"E4");var subQ18=sQuery(id+"F2.wireOp",EDGE,"E12");var subQ19=makeQuery(id+"F3.boolean.opBoolean","COPY",FACE,{"derivedFrom":makeQuery(id+"F3.opExtrude","SWEPT_FACE",FACE,{"disambiguationData":[OSD([subQ18])]})});var subQ21=sQuery(id+"F7.wireOp",EDGE,"E30");var subQ22=sQuery(id+"F7.wireOp",EDGE,"E29");var subQ24=sQuery(id+"F0.wireOp",EDGE,"E3");var subQ26=sQuery(id+"F7.wireOp",EDGE,"E31");Q4=makeQuery(id+"F20.boolean.opBoolean","SPLIT",FACE,{"disambiguationData":[TD([makeQuery(id+"F20.opExtrude","SWEPT_FACE",FACE,{"disambiguationData":[OSD([sQuery(id+"F19.wireOp",EDGE,"E71.3.0.6")])]})])],"derivedFrom":makeQuery(id+"F18.boolean.opBoolean","SPLIT",FACE,{"disambiguationData":[TD([subQ19])],"derivedFrom":makeQuery(id+"F15.boolean.opBoolean","SPLIT",FACE,{"disambiguationData":[TD([subQ5])],"derivedFrom":makeQuery(id+"F8.boolean.opBoolean","MERGE",FACE,{"derivedFrom":[makeQuery(id+"F11.boolean.opBoolean","SPLIT",FACE,{"disambiguationData":[TD([subQ5])],"derivedFrom":makeQuery(id+"F1.opExtrude","SWEPT_FACE",FACE,{"disambiguationData":[OSD([subQ24])]})}),makeQuery(id+"F8.opLoft","SWEPT_FACE",FACE,{"disambiguationData":[OSD([subQ4,subQ24,subQ14,subQ22,subQ21,subQ26])]})]})})})});}
            var Q5;
            {var subQ0=sQuery(id+"F0.wireOp",EDGE,"E10.MirrorCS");var subQ1=sQuery(id+"F0.wireOp",EDGE,"E9.MirrorCS");var subQ2=sQuery(id+"F0.wireOp",EDGE,"E6.MirrorCS");Q5=makeQuery(id+"F20.boolean.opBoolean","SPLIT",FACE,{"disambiguationData":[TD([makeQuery(id+"F20.opExtrude","SWEPT_FACE",FACE,{"disambiguationData":[OSD([sQuery(id+"F19.wireOp",EDGE,"e9320bb9-dfa5-404e-80d7-207bc9714f88.3.0.0")])]})])],"derivedFrom":makeQuery(id+"F8.boolean.opBoolean","MERGE",FACE,{"derivedFrom":[makeQuery(id+"F11.boolean.opBoolean","SPLIT",FACE,{"disambiguationData":[TD([makeQuery(id+"F1.opExtrude","SWEPT_FACE",FACE,{"disambiguationData":[OSD([subQ2])]})])],"derivedFrom":makeQuery(id+"F1.opExtrude","SWEPT_FACE",FACE,{"disambiguationData":[OSD([subQ1])]})}),makeQuery(id+"F8.opLoft","SWEPT_FACE",FACE,{"disambiguationData":[OSD([subQ2,subQ1,subQ0,sQuery(id+"F7.wireOp",EDGE,"E36"),sQuery(id+"F7.wireOp",EDGE,"E37"),sQuery(id+"F7.wireOp",EDGE,"E38")])]})]})});}
            var Q6;
            {var subQ0=sQuery(id+"F0.wireOp",EDGE,"E10.MirrorCS");var subQ1=sQuery(id+"F0.wireOp",EDGE,"E9.MirrorCS");var subQ2=sQuery(id+"F0.wireOp",EDGE,"E6.MirrorCS");Q6=makeQuery(id+"F20.boolean.opBoolean","SPLIT",FACE,{"disambiguationData":[TD([makeQuery(id+"F20.opExtrude","SWEPT_FACE",FACE,{"disambiguationData":[OSD([sQuery(id+"F19.wireOp",EDGE,"e9320bb9-dfa5-404e-80d7-207bc9714f88.4.0.0")])]})])],"derivedFrom":makeQuery(id+"F8.boolean.opBoolean","MERGE",FACE,{"derivedFrom":[makeQuery(id+"F11.boolean.opBoolean","SPLIT",FACE,{"disambiguationData":[TD([makeQuery(id+"F1.opExtrude","SWEPT_FACE",FACE,{"disambiguationData":[OSD([subQ2])]})])],"derivedFrom":makeQuery(id+"F1.opExtrude","SWEPT_FACE",FACE,{"disambiguationData":[OSD([subQ1])]})}),makeQuery(id+"F8.opLoft","SWEPT_FACE",FACE,{"disambiguationData":[OSD([subQ2,subQ1,subQ0,sQuery(id+"F7.wireOp",EDGE,"E36"),sQuery(id+"F7.wireOp",EDGE,"E37"),sQuery(id+"F7.wireOp",EDGE,"E38")])]})]})});}
            var Q7;
            {var subQ4=sQuery(id+"F0.wireOp",EDGE,"E2");var subQ5=makeQuery(id+"F1.opExtrude","SWEPT_FACE",FACE,{"disambiguationData":[OSD([subQ4])]});var subQ14=sQuery(id+"F0.wireOp",EDGE,"E4");var subQ18=sQuery(id+"F2.wireOp",EDGE,"E12");var subQ19=makeQuery(id+"F3.boolean.opBoolean","COPY",FACE,{"derivedFrom":makeQuery(id+"F3.opExtrude","SWEPT_FACE",FACE,{"disambiguationData":[OSD([subQ18])]})});var subQ21=sQuery(id+"F7.wireOp",EDGE,"E30");var subQ22=sQuery(id+"F7.wireOp",EDGE,"E29");var subQ24=sQuery(id+"F0.wireOp",EDGE,"E3");var subQ26=sQuery(id+"F7.wireOp",EDGE,"E31");Q7=makeQuery(id+"F20.boolean.opBoolean","SPLIT",FACE,{"disambiguationData":[TD([makeQuery(id+"F20.opExtrude","SWEPT_FACE",FACE,{"disambiguationData":[OSD([sQuery(id+"F19.wireOp",EDGE,"E71.4.0.6")])]})])],"derivedFrom":makeQuery(id+"F18.boolean.opBoolean","SPLIT",FACE,{"disambiguationData":[TD([subQ19])],"derivedFrom":makeQuery(id+"F15.boolean.opBoolean","SPLIT",FACE,{"disambiguationData":[TD([subQ5])],"derivedFrom":makeQuery(id+"F8.boolean.opBoolean","MERGE",FACE,{"derivedFrom":[makeQuery(id+"F11.boolean.opBoolean","SPLIT",FACE,{"disambiguationData":[TD([subQ5])],"derivedFrom":makeQuery(id+"F1.opExtrude","SWEPT_FACE",FACE,{"disambiguationData":[OSD([subQ24])]})}),makeQuery(id+"F8.opLoft","SWEPT_FACE",FACE,{"disambiguationData":[OSD([subQ4,subQ24,subQ14,subQ22,subQ21,subQ26])]})]})})})});}
            var Q8;
            {var subQ0=sQuery(id+"F0.wireOp",EDGE,"E10.MirrorCS");var subQ1=sQuery(id+"F0.wireOp",EDGE,"E9.MirrorCS");var subQ2=sQuery(id+"F0.wireOp",EDGE,"E6.MirrorCS");Q8=makeQuery(id+"F20.boolean.opBoolean","SPLIT",FACE,{"disambiguationData":[TD([makeQuery(id+"F20.opExtrude","SWEPT_FACE",FACE,{"disambiguationData":[OSD([sQuery(id+"F19.wireOp",EDGE,"e9320bb9-dfa5-404e-80d7-207bc9714f88.5.0.0")])]})])],"derivedFrom":makeQuery(id+"F8.boolean.opBoolean","MERGE",FACE,{"derivedFrom":[makeQuery(id+"F11.boolean.opBoolean","SPLIT",FACE,{"disambiguationData":[TD([makeQuery(id+"F1.opExtrude","SWEPT_FACE",FACE,{"disambiguationData":[OSD([subQ2])]})])],"derivedFrom":makeQuery(id+"F1.opExtrude","SWEPT_FACE",FACE,{"disambiguationData":[OSD([subQ1])]})}),makeQuery(id+"F8.opLoft","SWEPT_FACE",FACE,{"disambiguationData":[OSD([subQ2,subQ1,subQ0,sQuery(id+"F7.wireOp",EDGE,"E36"),sQuery(id+"F7.wireOp",EDGE,"E37"),sQuery(id+"F7.wireOp",EDGE,"E38")])]})]})});}
            var Q9;
            {var subQ0=sQuery(id+"F0.wireOp",EDGE,"E10.MirrorCS");var subQ1=sQuery(id+"F0.wireOp",EDGE,"E9.MirrorCS");var subQ2=sQuery(id+"F0.wireOp",EDGE,"E6.MirrorCS");Q9=makeQuery(id+"F20.boolean.opBoolean","SPLIT",FACE,{"disambiguationData":[TD([makeQuery(id+"F20.opExtrude","SWEPT_FACE",FACE,{"disambiguationData":[OSD([sQuery(id+"F19.wireOp",EDGE,"e9320bb9-dfa5-404e-80d7-207bc9714f88.6.0.0")])]})])],"derivedFrom":makeQuery(id+"F8.boolean.opBoolean","MERGE",FACE,{"derivedFrom":[makeQuery(id+"F11.boolean.opBoolean","SPLIT",FACE,{"disambiguationData":[TD([makeQuery(id+"F1.opExtrude","SWEPT_FACE",FACE,{"disambiguationData":[OSD([subQ2])]})])],"derivedFrom":makeQuery(id+"F1.opExtrude","SWEPT_FACE",FACE,{"disambiguationData":[OSD([subQ1])]})}),makeQuery(id+"F8.opLoft","SWEPT_FACE",FACE,{"disambiguationData":[OSD([subQ2,subQ1,subQ0,sQuery(id+"F7.wireOp",EDGE,"E36"),sQuery(id+"F7.wireOp",EDGE,"E37"),sQuery(id+"F7.wireOp",EDGE,"E38")])]})]})});}
            var Q10;
            {var subQ1=sQuery(id+"F7.wireOp",EDGE,"E30");var subQ2=sQuery(id+"F7.wireOp",EDGE,"E29");var subQ4=sQuery(id+"F0.wireOp",EDGE,"E3");var subQ5=sQuery(id+"F0.wireOp",EDGE,"E2");var subQ7=sQuery(id+"F7.wireOp",EDGE,"E31");var subQ9=sQuery(id+"F0.wireOp",EDGE,"E4");Q10=makeQuery(id+"F20.boolean.opBoolean","SPLIT",FACE,{"disambiguationData":[TD([makeQuery(id+"F20.opExtrude","SWEPT_FACE",FACE,{"disambiguationData":[OSD([sQuery(id+"F19.wireOp",EDGE,"E71.6.0.6")])]})])],"derivedFrom":makeQuery(id+"F15.boolean.opBoolean","SPLIT",FACE,{"disambiguationData":[TD([makeQuery(id+"F8.opLoft","CAP_FACE",FACE,{"disambiguationData":[OSD([makeQuery(id+"F7.imprint","IMPRINT",FACE,{"disambiguationData":[TD([[makeQuery(id+"F7.imprint","IMPRINT",EDGE,{"derivedFrom":subQ2}),1.0]])]})])],"isStart":true})])],"derivedFrom":makeQuery(id+"F8.boolean.opBoolean","MERGE",FACE,{"derivedFrom":[makeQuery(id+"F11.boolean.opBoolean","SPLIT",FACE,{"disambiguationData":[TD([makeQuery(id+"F1.opExtrude","SWEPT_FACE",FACE,{"disambiguationData":[OSD([subQ5])]})])],"derivedFrom":makeQuery(id+"F1.opExtrude","SWEPT_FACE",FACE,{"disambiguationData":[OSD([subQ4])]})}),makeQuery(id+"F8.opLoft","SWEPT_FACE",FACE,{"disambiguationData":[OSD([subQ5,subQ4,subQ9,subQ2,subQ1,subQ7])]})]})})});}
            extrude(context, id + "F21", {"entities" : qUnion([Q0, Q1, Q2, Q3, Q4, Q5, Q6, Q7, Q8, Q9, Q10]), "operationType" : NewBodyOperationType.REMOVE, "endBound" : BoundingType.THROUGH_ALL, "oppositeDirection" : true, "depth" : 25.4 * mm});
        }
    });
